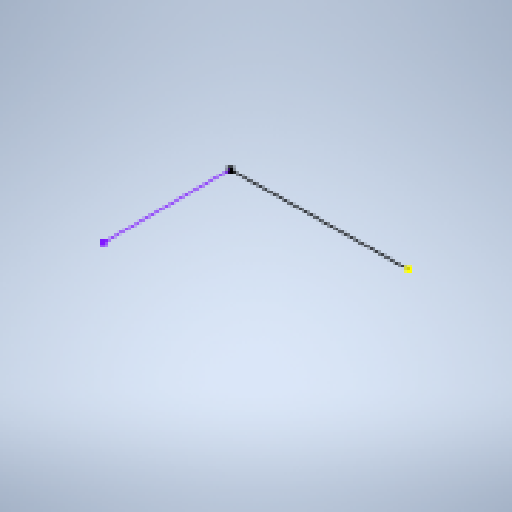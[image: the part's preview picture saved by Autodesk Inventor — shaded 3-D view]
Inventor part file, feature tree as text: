
AUTODESK INVENTOR PART (.ipt)
format: ipt  version: 2025 (Build 290162000, 162)  size: 150,528 bytes
history: native  units: in
note: dims shown in document units (in); Inventor stores cm internally (conversion verified against a paired STEP export)
features: other x2, plane x1, sketch x1
ambient origin geometry x8: Origin, YZ Plane, XZ Plane, XY Plane, X Axis, Y Axis, Z Axis, Center Point
feature tree (4):
  other  "Work Point1"
  other  "Work Point2"
  plane  "Work Plane1"
  sketch  "3D Sketch1"
